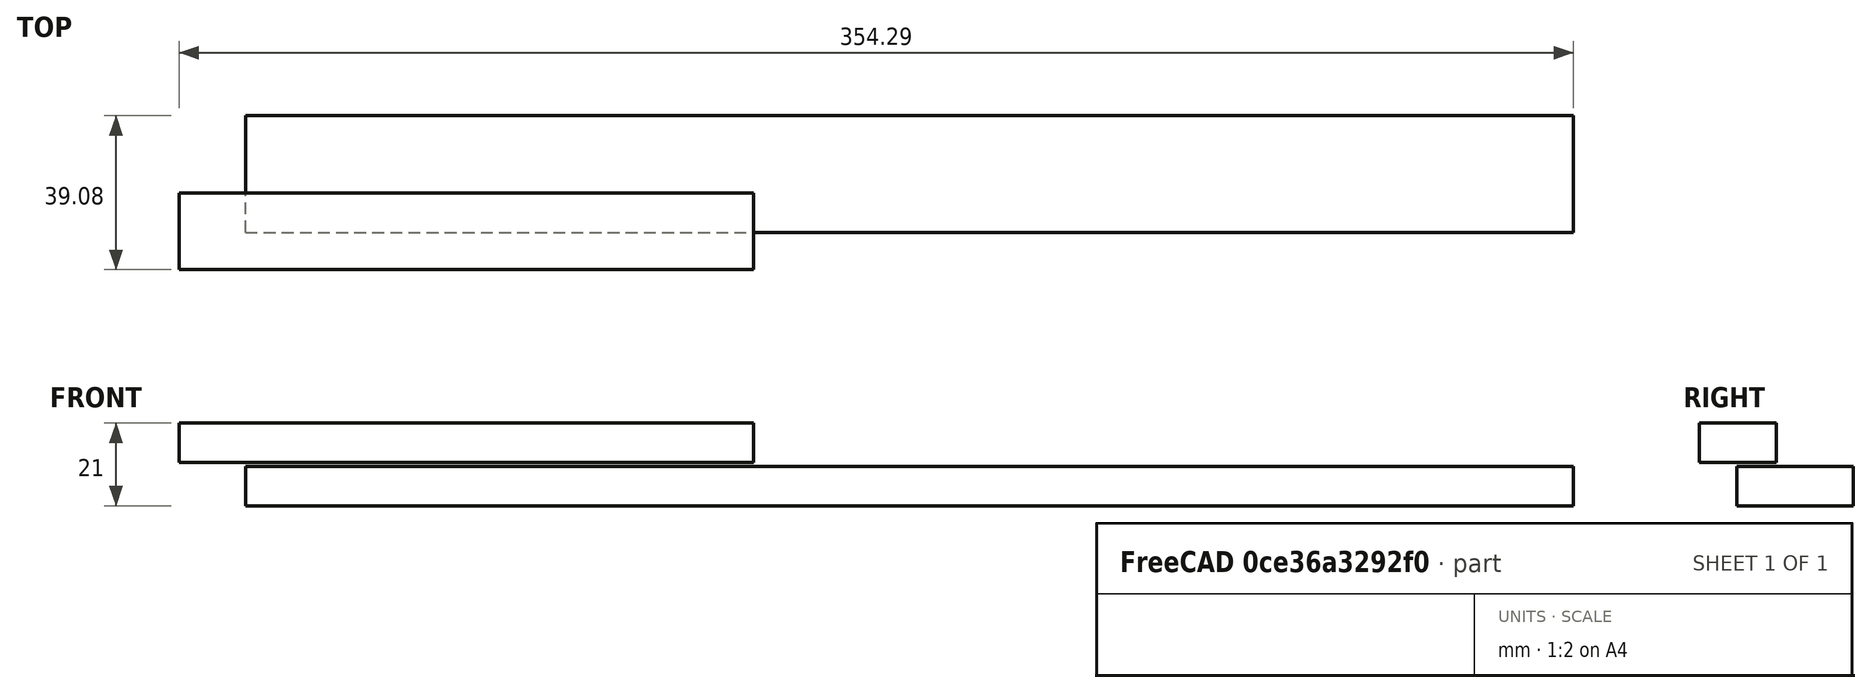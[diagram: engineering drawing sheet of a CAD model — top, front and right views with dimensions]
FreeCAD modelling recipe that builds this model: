
FCSTD DOCUMENT  (FreeCAD 0.18R16146 (Git))
Label: degemerMat3
License: All rights reserved
LicenseURL: http://en.wikipedia.org/wiki/All_rights_reserved
objects: Path::FeaturePython×3, Part::Part2DObjectPython×2, Sketcher::SketchObject×1, PartDesign::Pad×1, PartDesign::Body×1, App::FeaturePython×1, App::DocumentObjectGroup×1, Part::FeaturePython×1, Path::FeatureCompoundPython×1, Mesh::FeaturePython×1
note: 7 computed .brp shape members not serialized (recipe doc carries the construction recipe); baked Part::Feature solids carry a one-line shape summary decoded from their .brp

FEATURE [Sketcher::SketchObject] Sketch
  MapMode = 5
  Support = -> [XY_Plane]
  sketch-geometry (4):
    g0: LineSegment StartX=-16.9276 StartY=10.0019 StartZ=0 EndX=129.053 EndY=10.0019 EndZ=0
    g1: LineSegment StartX=129.053 StartY=10.0019 StartZ=0 EndX=129.053 EndY=-9.48325 EndZ=0
    g2: LineSegment StartX=129.053 StartY=-9.48325 StartZ=0 EndX=-16.9276 EndY=-9.48325 EndZ=0
    g3: LineSegment StartX=-16.9276 StartY=-9.48325 StartZ=0 EndX=-16.9276 EndY=10.0019 EndZ=0
  constraints (8):
    c: Coincident(g0,g1)
    c: Coincident(g1,g2)
    c: Coincident(g2,g3)
    c: Coincident(g3,g0)
    c: Horizontal(g0)
    c: Horizontal(g2)
    c: Vertical(g1)
    c: Vertical(g3)
FEATURE [PartDesign::Pad] Pad
  Length = 10
  Length2 = 100
  Profile = -> Sketch
  Type = 0
FEATURE [PartDesign::Body] Body
  Group = -> [Sketch,Pad]
  Origin = -> Origin
  Tip = -> Pad
FEATURE [Part::Part2DObjectPython] ShapeString  # Draft 2D object (typed FeaturePython)
  FontFile = <userpath>/.local/share/fonts/CamBamStickFonts/1CamBam_Stick_1.ttf
  Placement = pos=(-14.65,-3.18,10) rot=(0,0,-1;0rad)
  Size = 10
  String = Degemer Mat
  Support = -> [Pad]
  Tracking = 5
FEATURE [App::FeaturePython] SetupSheet  # Path/CAM operation (typed FeaturePython)
  ClearanceHeightExpression = OpStockZMax+SetupSheet.ClearanceHeightOffset
  ClearanceHeightOffset = 5
  FinalDepthExpression = OpFinalDepth
  HorizRapid = 0
  SafeHeightExpression = OpStockZMax+SetupSheet.SafeHeightOffset
  SafeHeightOffset = 3
  StartDepthExpression = OpStartDepth
  StepDownExpression = OpToolDiameter
  VertRapid = 0
FEATURE [Part::Part2DObjectPython] Clone2D  label="Model-ShapeString"  # Draft 2D object (typed FeaturePython)
  Fuse = false
  Objects = -> [ShapeString]
  PathResource = Model
  Placement = pos=(-0.436697,3.11376,-1) rot=(0,0,-1;0rad)
  Scale = (1,1,1)
FEATURE [App::DocumentObjectGroup] Model
  Group = -> [Clone2D]
FEATURE [Path::FeaturePython] Default_Tool  label="Default Tool"  # Path/CAM operation (typed FeaturePython)
  HorizFeed = 8
  HorizRapid = 0
  SpindleDir = 0
  SpindleSpeed = 0
  ToolNumber = 1
  VertFeed = 5
  VertRapid = 0
  expr: HorizRapid = SetupSheet.HorizRapid
  expr: VertRapid = SetupSheet.VertRapid
FEATURE [Part::FeaturePython] Stock  # WARN: FeaturePython — macro-defined, semantics opaque (R4)
  Base = -> Model
  ExtXneg = 1
  ExtXpos = 1
  ExtYneg = 1
  ExtYpos = 1
  ExtZneg = 10
  ExtZpos = 0
  Placement = pos=(1,1,-1) rot=(0,0,1;0rad)
  StockType = FromBase
FEATURE [Path::FeaturePython] Engrave  # Path/CAM operation (typed FeaturePython)
  Active = true
  ClearanceHeight = 4
  FinalDepth = -2
  OpFinalDepth = -3
  OpStartDepth = -1
  OpStockZMax = -1
  OpStockZMin = -11
  OpToolDiameter = 3
  SafeHeight = 2
  StartDepth = 0
  StartVertex = 0
  StepDown = 2
  ToolController = -> Default_Tool
  expr: ClearanceHeight = OpStockZMax + SetupSheet.ClearanceHeightOffset
  expr: SafeHeight = OpStockZMax + SetupSheet.SafeHeightOffset
  expr: StepDown = 2
  expr: FinalDepth = -2
  expr: StartDepth = 0
FEATURE [Path::FeatureCompoundPython] Operations  # Path/CAM operation (typed FeaturePython)
  Group = -> [Engrave]
  UsePlacements = false
FEATURE [Path::FeaturePython] Job  # Path/CAM operation (typed FeaturePython)
  GeometryTolerance = 0.01
  Model = -> Model
  Operations = -> Operations
  PostProcessor = 10
  PostProcessorOutputFile = <userpath>/dev/CNC/MiscCNC/degemerMat3.gcode
  SetupSheet = -> SetupSheet
  Stock = -> Stock
  ToolController = -> [Default_Tool]
FEATURE [Mesh::FeaturePython] CutMaterial  # WARN: FeaturePython — macro-defined, semantics opaque (R4)
